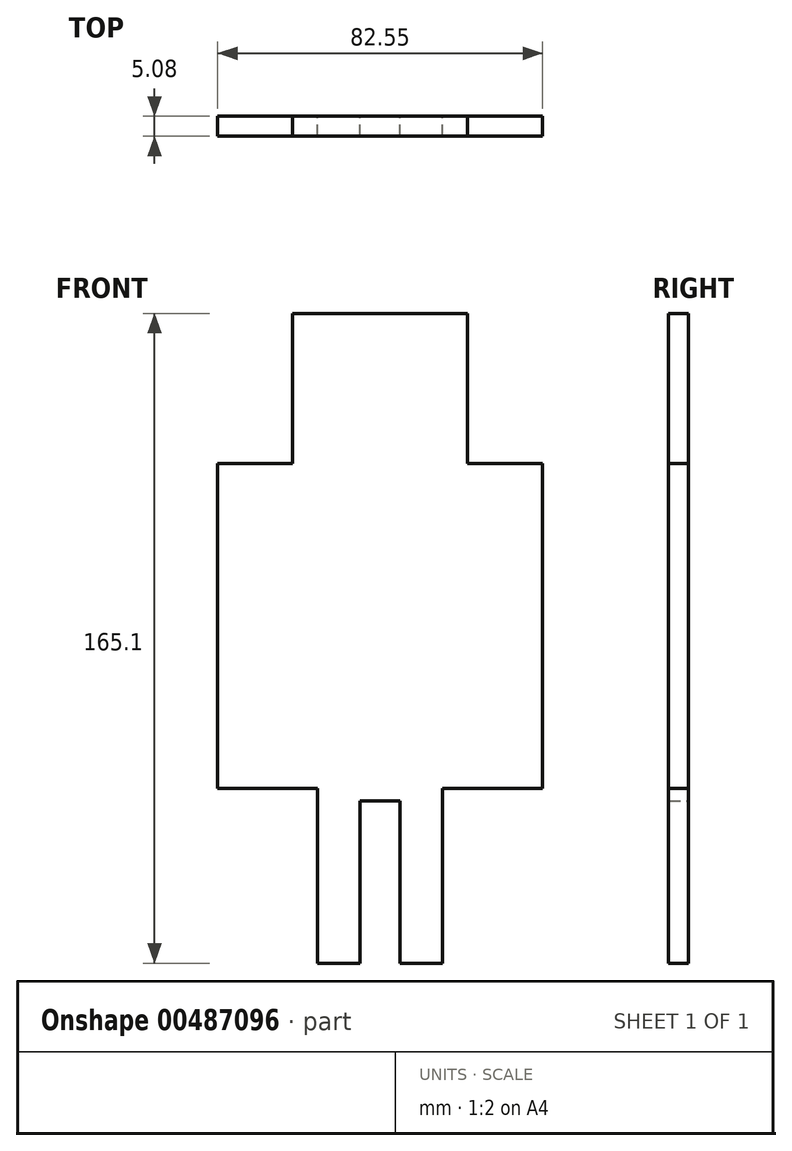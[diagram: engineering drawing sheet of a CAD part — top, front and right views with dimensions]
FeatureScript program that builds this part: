
annotation { "Feature Type Name" : "Feature", "Feature Type Description" : "" }
export const myFeature = defineFeature(function(context is Context, id is Id, definition is map)
    precondition{}
    {
        {
            var Q0;
            Q0=qCreatedBy(makeId("Front.planeOp"),FACE);
            var sketch = newSketch(context, id + "F0", { "sketchPlane" : qUnion([Q0])});
            skLineSegment(sketch, "E0.bottom", {"start": v(-17.15, 97.56) * mm, "end": v(27.3, 97.56) * mm});
            skLineSegment(sketch, "E0.top", {"start": v(-10.8, -67.54) * mm, "end": v(0, -67.54) * mm});
            skLineSegment(sketch, "E0.left", {"start": v(-36.2, 59.46) * mm, "end": v(-36.2, -23.1) * mm});
            skLineSegment(sketch, "E0.right", {"start": v(46.35, 59.46) * mm, "end": v(46.36, -23.1) * mm});
            skLineSegment(sketch, "E1.top", {"start": v(-36.2, 59.46) * mm, "end": v(-17.15, 59.46) * mm});
            skLineSegment(sketch, "E1.right", {"start": v(-17.15, 97.56) * mm, "end": v(-17.15, 59.46) * mm});
            skLineSegment(sketch, "E2.top", {"start": v(46.36, 59.46) * mm, "end": v(27.3, 59.46) * mm});
            skLineSegment(sketch, "E2.right", {"start": v(27.3, 97.56) * mm, "end": v(27.3, 59.46) * mm});
            skLineSegment(sketch, "E3.top", {"start": v(-36.2, -23.1) * mm, "end": v(-10.8, -23.1) * mm});
            skLineSegment(sketch, "E3.right", {"start": v(-10.8, -67.54) * mm, "end": v(-10.8, -23.1) * mm});
            skLineSegment(sketch, "E4.top", {"start": v(46.36, -23.1) * mm, "end": v(20.95, -23.1) * mm});
            skLineSegment(sketch, "E4.right", {"start": v(20.96, -67.54) * mm, "end": v(20.95, -23.1) * mm});
            skLineSegment(sketch, "E5.bottom", {"start": v(0, -26.27) * mm, "end": v(10.16, -26.27) * mm});
            skLineSegment(sketch, "E5.left", {"start": v(0, -26.27) * mm, "end": v(0, -67.54) * mm});
            skLineSegment(sketch, "E5.right", {"start": v(10.16, -26.27) * mm, "end": v(10.16, -67.54) * mm});
            skLineSegment(sketch, "E6.trimOffspring", {"start": v(10.16, -67.54) * mm, "end": v(20.96, -67.54) * mm});
            skSolve(sketch);
        }
        {
            var Q0;
            Q0 = qSketchRegion(id + "F0", true);
            extrude(context, id + "F1", {"entities" : qUnion([Q0]), "depth" : 5.08 * mm});
        }
    });
